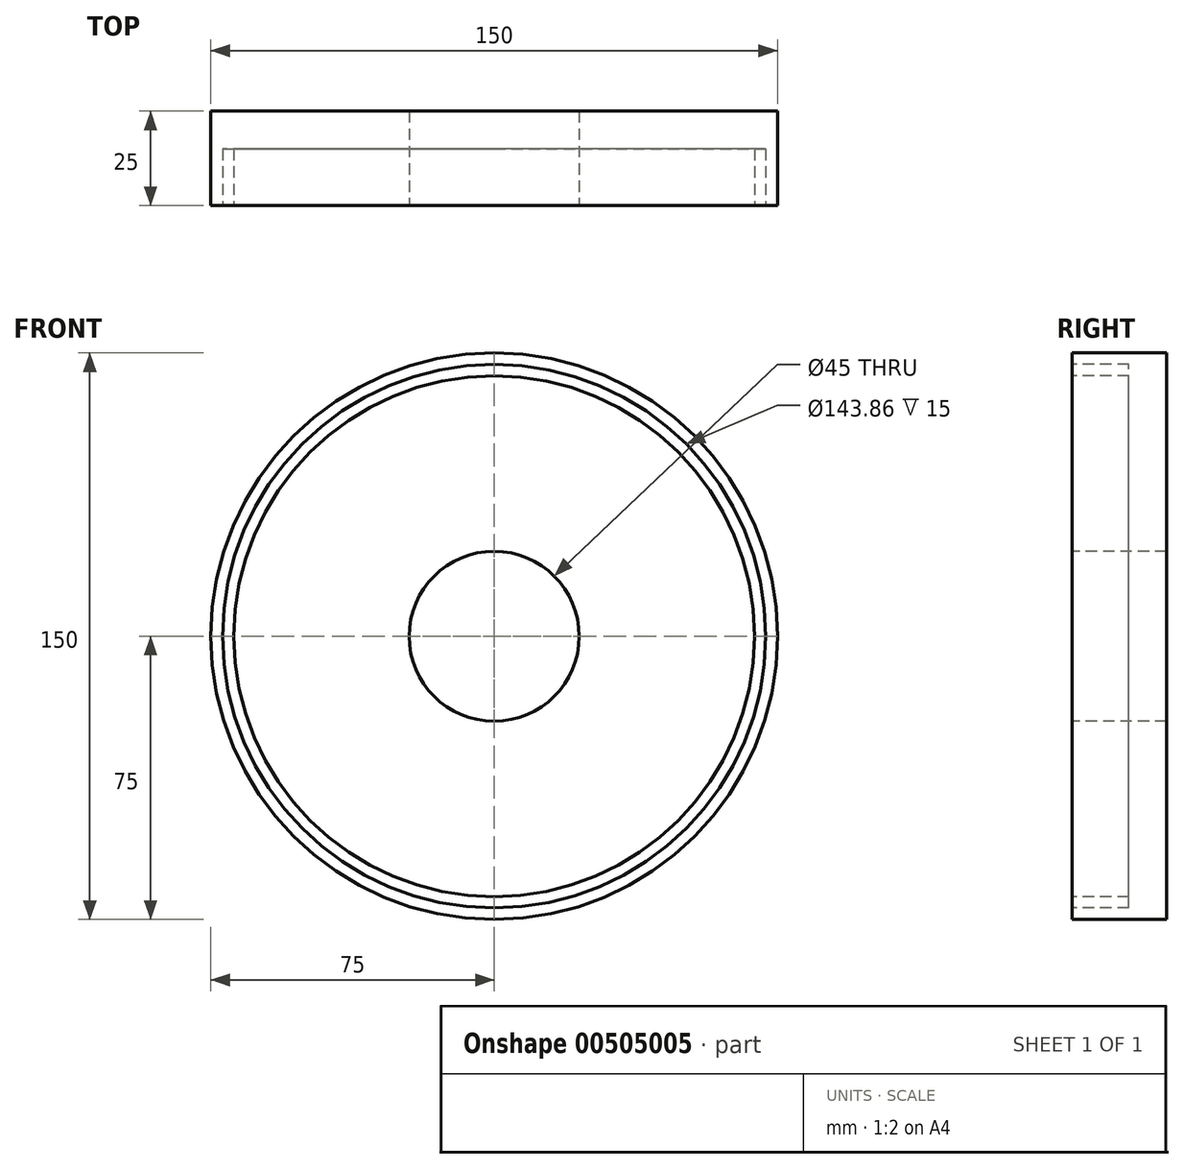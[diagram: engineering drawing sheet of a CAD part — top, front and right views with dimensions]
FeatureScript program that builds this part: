
annotation { "Feature Type Name" : "Feature", "Feature Type Description" : "" }
export const myFeature = defineFeature(function(context is Context, id is Id, definition is map)
    precondition{}
    {
        {
            var Q0;
            Q0=qCreatedBy(makeId("Front.planeOp"),FACE);
            var sketch = newSketch(context, id + "F0", { "sketchPlane" : qUnion([Q0])});
            skCircle(sketch, "E0", {"center": v(0, 0) * mm, "radius": 75 * mm});
            skCircle(sketch, "E1", {"center": v(0, 0) * mm, "radius": 20.67 * mm});
            skSolve(sketch);
        }
        {
            var Q0;
            Q0=makeQuery(id+"F0.imprint","IMPRINT",FACE,{"disambiguationData":[TD([[makeQuery(id+"F0.imprint","IMPRINT",EDGE,{"derivedFrom":sQuery(id+"F0.wireOp",EDGE,"E0")}),1.0]])]});
            var Q1;
            Q1=makeQuery(id+"F0.imprint","IMPRINT",FACE,{"disambiguationData":[TD([[makeQuery(id+"F0.imprint","IMPRINT",EDGE,{"derivedFrom":sQuery(id+"F0.wireOp",EDGE,"E1")}),1.0]])]});
            extrude(context, id + "F1", {"entities" : qUnion([Q0, Q1]), "depth" : 25 * mm});
        }
        {
            var Q0;
            Q0=makeQuery(id+"F1.opExtrude","CAP_FACE",FACE,{"disambiguationData":[OSD([sQuery(id+"F0.wireOp",EDGE,"E0")])],"isStart":false});
            var sketch = newSketch(context, id + "F2", { "sketchPlane" : qUnion([Q0])});
            skCircle(sketch, "E2", {"center": v(0, 0) * mm, "radius": 22.5 * mm});
            skSolve(sketch);
        }
        {
            var Q0;
            Q0=makeQuery(id+"F2.imprint","IMPRINT",FACE,{"disambiguationData":[TD([[makeQuery(id+"F2.imprint","IMPRINT",EDGE,{"derivedFrom":sQuery(id+"F2.wireOp",EDGE,"E2")}),1.0]])]});
            var Q1;
            Q1=sQuery(id+"F2.wireOp",EDGE,"E2");
            extrude(context, id + "F3", {"entities" : qUnion([Q0]), "operationType" : NewBodyOperationType.REMOVE, "surfaceEntities" : qUnion([Q1]), "endBound" : BoundingType.THROUGH_ALL, "oppositeDirection" : true, "depth" : 25 * mm});
        }
        {
            var Q0;
            Q0=makeQuery(id+"F1.opExtrude","CAP_FACE",FACE,{"disambiguationData":[OSD([sQuery(id+"F0.wireOp",EDGE,"E0")])],"isStart":false});
            var sketch = newSketch(context, id + "F4", { "sketchPlane" : qUnion([Q0])});
            skCircle(sketch, "E3", {"center": v(0, 0) * mm, "radius": 71.93 * mm});
            skCircle(sketch, "E4.0", {"center": v(0, 0) * mm, "radius": 68.93 * mm});
            skSolve(sketch);
        }
        {
            var Q0;
            Q0=makeQuery(id+"F4.imprint","IMPRINT",FACE,{"disambiguationData":[TD([[makeQuery(id+"F4.imprint","IMPRINT",EDGE,{"derivedFrom":sQuery(id+"F4.wireOp",EDGE,"E3")}),1.0]])]});
            extrude(context, id + "F5", {"entities" : qUnion([Q0]), "operationType" : NewBodyOperationType.REMOVE, "oppositeDirection" : true, "depth" : 15 * mm});
        }
    });
